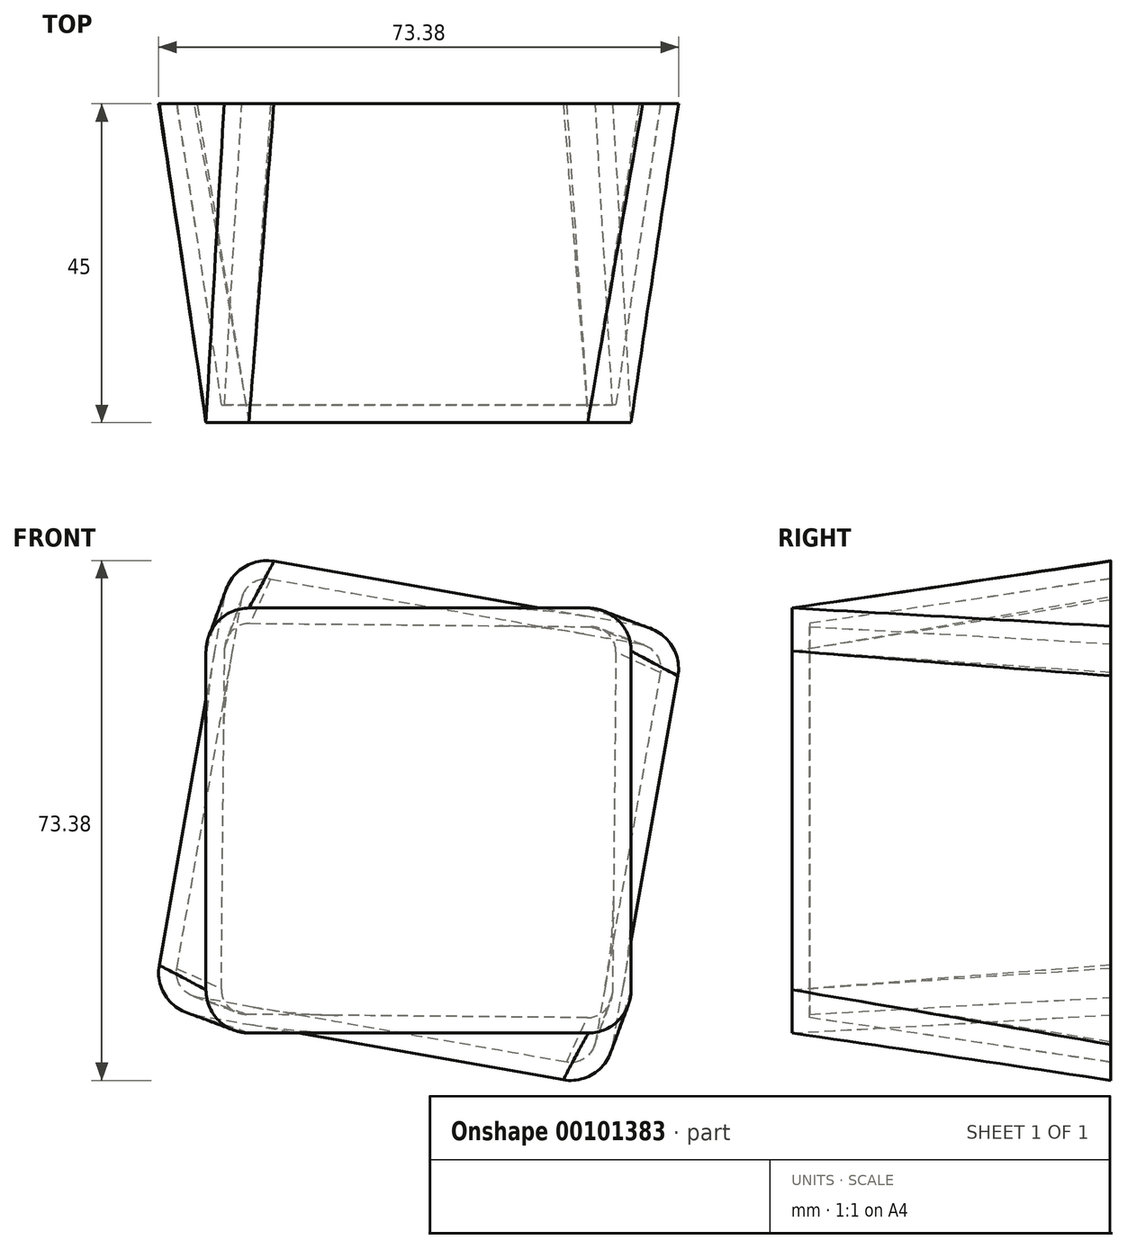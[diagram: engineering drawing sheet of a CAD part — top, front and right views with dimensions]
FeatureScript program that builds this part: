
annotation { "Feature Type Name" : "Feature", "Feature Type Description" : "" }
export const myFeature = defineFeature(function(context is Context, id is Id, definition is map)
    precondition{}
    {
        {
            var Q0;
            Q0=qCreatedBy(makeId("Front.planeOp"),FACE);
            var sketch = newSketch(context, id + "F0", { "sketchPlane" : qUnion([Q0])});
            skLineSegment(sketch, "E0.bottom", {"start": v(-30, 30) * mm, "end": v(30, 30) * mm});
            skLineSegment(sketch, "E0.top", {"start": v(-30, -30) * mm, "end": v(30, -30) * mm});
            skLineSegment(sketch, "E0.left", {"start": v(-30, 30) * mm, "end": v(-30, -30) * mm});
            skLineSegment(sketch, "E0.right", {"start": v(30, 30) * mm, "end": v(30, -30) * mm});
            skPoint(sketch, "E0.middle", {"position": v(0, 0) * mm});
            skSolve(sketch);
        }
        {
            var Q0;
            Q0=qCreatedBy(makeId("Front.planeOp"),FACE);
            cPlane(context, id + "F1", {"entities" : qUnion([Q0]), "cplaneType" : CPlaneType.OFFSET, "offset" : 45 * mm, "oppositeDirection" : true, "width" : 150 * mm, "height" : 150 * mm});
        }
        {
            var Q0;
            Q0=qCreatedBy(id+"F1.planeOp",FACE);
            var sketch = newSketch(context, id + "F2", { "sketchPlane" : qUnion([Q0])});
            skLineSegment(sketch, "E1", {"start": v(-26.36, 37.65) * mm, "end": v(-37.65, -26.36) * mm});
            skLineSegment(sketch, "E2", {"start": v(-37.65, -26.36) * mm, "end": v(26.36, -37.65) * mm});
            skLineSegment(sketch, "E3", {"start": v(26.36, -37.65) * mm, "end": v(37.65, 26.36) * mm});
            skLineSegment(sketch, "E4", {"start": v(37.65, 26.36) * mm, "end": v(-26.36, 37.65) * mm});
            skLineSegment(sketch, "E5", {"start": v(-26.36, 37.65) * mm, "end": v(26.36, -37.65) * mm});
            skLineSegment(sketch, "E6", {"start": v(-37.65, -26.36) * mm, "end": v(37.65, 26.36) * mm});
            skSolve(sketch);
        }
        {
            var Q0;
            Q0 = qSketchRegion(id + "F0", true);
            var Q1;
            Q1 = qSketchRegion(id + "F2", true);
            loft(context, id + "F3", {"sheetProfilesArray" : [{ "sheetProfileEntities" : qUnion([Q0]) }, { "sheetProfileEntities" : qUnion([Q1]) }]});
        }
        {
            var Q0;
            Q0=makeQuery(id+"F3.opLoft","SWEPT_EDGE",EDGE,{"disambiguationData":[OSD([sQuery(id+"F0.wireOp",EDGE,"E0.bottom"),sQuery(id+"F0.wireOp",EDGE,"E0.left"),sQuery(id+"F2.wireOp",EDGE,"E1"),sQuery(id+"F2.wireOp",EDGE,"E4"),sQuery(id+"F2.wireOp",EDGE,"E5")])]});
            var Q1;
            Q1=makeQuery(id+"F3.opLoft","SWEPT_EDGE",EDGE,{"disambiguationData":[OSD([sQuery(id+"F0.wireOp",EDGE,"E0.bottom"),sQuery(id+"F0.wireOp",EDGE,"E0.right"),sQuery(id+"F2.wireOp",EDGE,"E3"),sQuery(id+"F2.wireOp",EDGE,"E4"),sQuery(id+"F2.wireOp",EDGE,"E6")])]});
            var Q2;
            Q2=makeQuery(id+"F3.opLoft","SWEPT_EDGE",EDGE,{"disambiguationData":[OSD([sQuery(id+"F0.wireOp",EDGE,"E0.top"),sQuery(id+"F0.wireOp",EDGE,"E0.right"),sQuery(id+"F2.wireOp",EDGE,"E2"),sQuery(id+"F2.wireOp",EDGE,"E3"),sQuery(id+"F2.wireOp",EDGE,"E5")])]});
            var Q3;
            Q3=makeQuery(id+"F3.opLoft","SWEPT_EDGE",EDGE,{"disambiguationData":[OSD([sQuery(id+"F0.wireOp",EDGE,"E0.top"),sQuery(id+"F0.wireOp",EDGE,"E0.left"),sQuery(id+"F2.wireOp",EDGE,"E1"),sQuery(id+"F2.wireOp",EDGE,"E2"),sQuery(id+"F2.wireOp",EDGE,"E6")])]});
            fillet(context, id + "F4", {"entities" : qUnion([Q0, Q1, Q2, Q3]), "radius" : 6 * mm, "tangentPropagation" : true, "allowEdgeOverflow" : false});
        }
        {
            var Q0;
            {var subQ0=sQuery(id+"F2.wireOp",EDGE,"E4");Q0=makeQuery(id+"F3.opLoft","CAP_FACE",FACE,{"disambiguationData":[OSD([makeQuery(id+"F2.imprint","IMPRINT",FACE,{"disambiguationData":[TD([[makeQuery(id+"F2.imprint","IMPRINT",EDGE,{"derivedFrom":subQ0}),1.0]])]})])],"isStart":true});}
            shell(context, id + "F5", {"entities" : qUnion([Q0]), "thickness" : 2.5 * mm});
        }
    });
